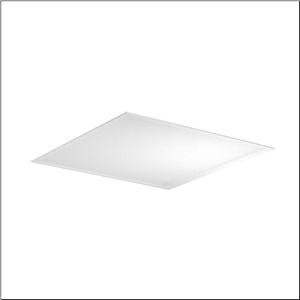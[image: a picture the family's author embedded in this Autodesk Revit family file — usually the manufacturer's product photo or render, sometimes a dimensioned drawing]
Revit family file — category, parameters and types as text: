
# Revit family: apollon_r__31_square_51mp12wd2442_6000
name_source: partatom
category: Lighting Fixtures
units: mm (PartAtom-declared; Revit-internal decimal feet)

## family parameters
Cut with Voids When Loaded = No
Host = Face
Light Source = No
Part Type = Normal
Room Calculation Point = No
Round Connector Dimension = Use Diameter
Shared = No

## types (1)
- Apollon® 31 square (1 x LED, 3800 lm, 27.5 W, 4000K)
    Apparent Load = 28 VA
    CIE Flux Codes = 61 87 97 100 100
    Color Rendering = 80
    Color Temperature = 4000K
    Default Elevation = 1800 mm
    Description = Apollon® 31 square, office luminaire, primary optical cover: micro prismatic cover, of PMMA, CAT 2 (L<= 3000cd/m²), light emission: direct distribution, primary light characteristic: symmetric, installation type: lay-in mounting, LED, rated luminous flux: 3.800lm, luminous efficacy: 138lm/W, light colour: 840, colour temperature: 4000K, with terminal, 5-pole, mains connection: 220..240V, AC/DC, 0/50..60Hz, rated input power: 28W, housing, of aluminium, traffic white (RAL 9016), module: M600, length: 595mm, width: 595mm, height: 32mm, housing upper side, of sheet steel, galvanised, protection rating (complete): IP20, protection rating (on room side): IP40, insulation class (complete): insulation class II (safety insulation), certification: CE, ENEC, impact resistance: IK03, permissible operating ambient temperature: -20..+40°C, permissible storage temperature: -20..+60°C, packaging unit: 1 piece
    Height = 0 mm  [stored 0 ft]
    Lamp = 1 x LED
    Lamp Light Flux = 3800 lm
    Lamp Power = 27.5 W
    Lamp count = 1
    Length = 595 mm
    Luminous efficacy = 138 lm/W
    Manufacturer = Siteco
    ModVariant = No
    Model = 51MP12WD2442
    Mounting Place = Ceiling
    Mounting Type = Recessed
    Number of Poles = 1
    OnlyDefault = Yes
    Power Factor = 1
    Product Name = Apollon® 31 square
    Product group = office luminaire | ceiling recessed
    ProductGroupID = 400
    Protection Class = Protection class II
    Protection Degree = IP 20
    RLX_Detail_Level = 1
    RLX_Emergency_Light_Flux = 0 lm
    RLX_Emergency_Type = 0
    RLX_Emergency_Type_DB = No
    RlxData = <blob elided: 12477 chars, md5=afae746e>
    Socket = socket
    Standby Power = 0 W
    System Light Flux = 3800 lm
    System Power = 28 W
    Type Comments = Product without accessories
    Type Image = l_1291035.jpg
    URL = http://relux.com
    VarID = ---
    Voltage = 0 V
    Weight = 0.00 kg
    Width = 595 mm

note: [stored X ft] marks values corroborated as IEEE doubles in the binary element streams (Revit-internal decimal feet)

## geometry (parser evidence)
native form markers: Sweep x12
no freeform markers — native parametric forms only
